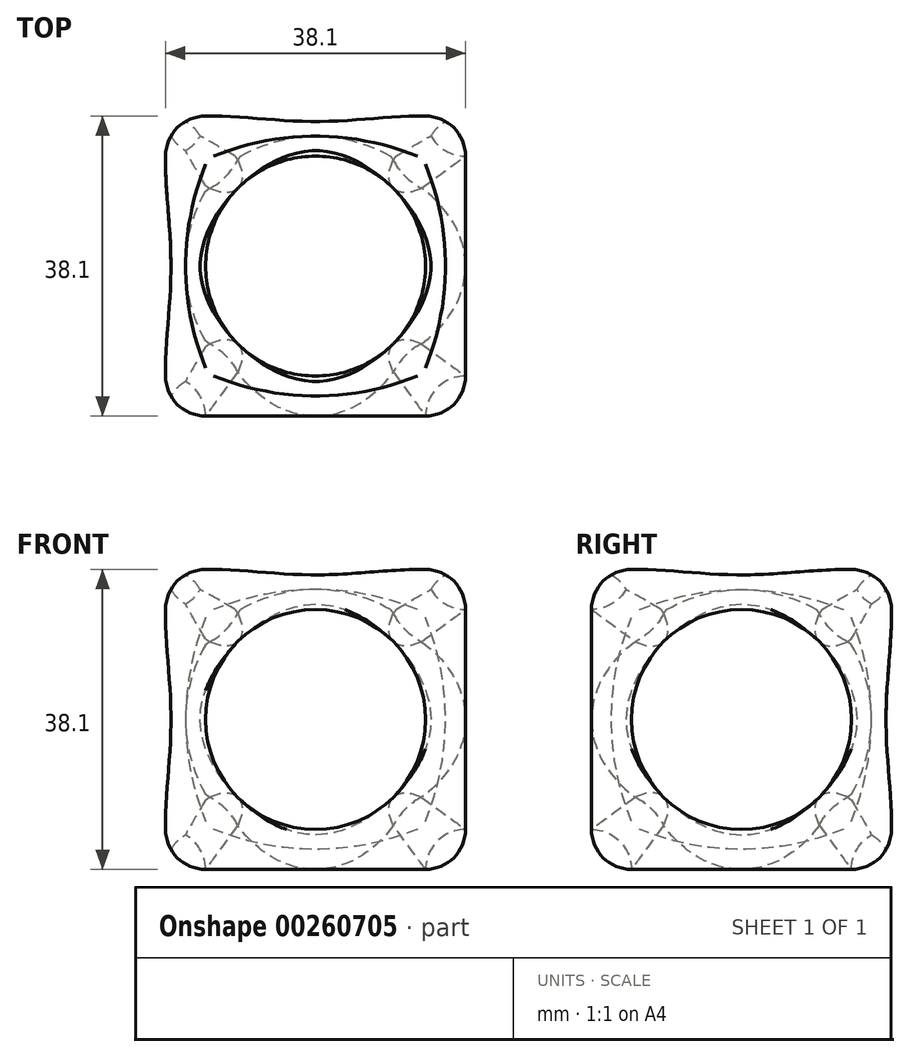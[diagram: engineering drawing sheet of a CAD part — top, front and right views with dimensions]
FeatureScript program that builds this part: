
annotation { "Feature Type Name" : "Feature", "Feature Type Description" : "" }
export const myFeature = defineFeature(function(context is Context, id is Id, definition is map)
    precondition{}
    {
        {
            var Q0;
            Q0=qCreatedBy(makeId("Front.planeOp"),FACE);
            var sketch = newSketch(context, id + "F0", { "sketchPlane" : qUnion([Q0])});
            skLineSegment(sketch, "E0.bottom", {"start": v(-19.05, 19.05) * mm, "end": v(19.05, 19.05) * mm});
            skLineSegment(sketch, "E0.top", {"start": v(-19.05, -19.05) * mm, "end": v(19.05, -19.05) * mm});
            skLineSegment(sketch, "E0.left", {"start": v(-19.05, 19.05) * mm, "end": v(-19.05, -19.05) * mm});
            skLineSegment(sketch, "E0.right", {"start": v(19.05, 19.05) * mm, "end": v(19.05, -19.05) * mm});
            skLineSegment(sketch, "E1", {"start": v(-19.05, 0) * mm, "end": v(0, 0) * mm});
            skLineSegment(sketch, "E2", {"start": v(0, 0) * mm, "end": v(19.05, 0) * mm});
            skLineSegment(sketch, "E3", {"start": v(0, 19.05) * mm, "end": v(0, 0) * mm});
            skLineSegment(sketch, "E4", {"start": v(0, -19.05) * mm, "end": v(0, 0) * mm});
            skSolve(sketch);
        }
        {
            var Q0;
            Q0 = qSketchRegion(id + "F0", true);
            extrude(context, id + "F1", {"entities" : qUnion([Q0]), "endBound" : BoundingType.SYMMETRIC, "depth" : 38.1 * mm});
        }
        {
            var Q0;
            Q0=makeQuery(id+"F1.opExtrude","CAP_FACE",FACE,{"disambiguationData":[OSD([sQuery(id+"F0.wireOp",EDGE,"E0.bottom"),sQuery(id+"F0.wireOp",EDGE,"E0.top"),sQuery(id+"F0.wireOp",EDGE,"E0.left"),sQuery(id+"F0.wireOp",EDGE,"E0.right")])],"isStart":false});
            var sketch = newSketch(context, id + "F2", { "sketchPlane" : qUnion([Q0])});
            skCircle(sketch, "E5", {"center": v(0, 0) * mm, "radius": 13.97 * mm});
            skPoint(sketch, "E5.first.point", {"position": v(0, -13.97) * mm});
            skPoint(sketch, "E5.second.point", {"position": v(-13.97, 0) * mm});
            skPoint(sketch, "E5.third.point", {"position": v(0, 13.97) * mm});
            skSolve(sketch);
        }
        {
            var Q0;
            Q0 = qSketchRegion(id + "F2", true);
            extrude(context, id + "F3", {"entities" : qUnion([Q0]), "operationType" : NewBodyOperationType.REMOVE, "oppositeDirection" : true, "depth" : 76.2 * mm});
        }
        {
            var Q0;
            Q0=makeQuery(id+"F1.opExtrude","SWEPT_FACE",FACE,{"disambiguationData":[OSD([sQuery(id+"F0.wireOp",EDGE,"E0.right")])]});
            var sketch = newSketch(context, id + "F4", { "sketchPlane" : qUnion([Q0])});
            skCircle(sketch, "E6", {"center": v(0, 0) * mm, "radius": 13.97 * mm});
            skPoint(sketch, "E6.first.point", {"position": v(0, -13.97) * mm});
            skPoint(sketch, "E6.second.point", {"position": v(-13.97, 0) * mm});
            skPoint(sketch, "E6.third.point", {"position": v(0, 13.97) * mm});
            skSolve(sketch);
        }
        {
            var Q0;
            Q0 = qSketchRegion(id + "F4", true);
            extrude(context, id + "F5", {"entities" : qUnion([Q0]), "operationType" : NewBodyOperationType.REMOVE, "oppositeDirection" : true, "depth" : 76.2 * mm});
        }
        {
            var Q0;
            Q0=makeQuery(id+"F1.opExtrude","SWEPT_FACE",FACE,{"disambiguationData":[OSD([sQuery(id+"F0.wireOp",EDGE,"E0.top")])]});
            var sketch = newSketch(context, id + "F6", { "sketchPlane" : qUnion([Q0])});
            skCircle(sketch, "E7", {"center": v(0, 0) * mm, "radius": 13.97 * mm});
            skPoint(sketch, "E7.first.point", {"position": v(0, -13.97) * mm});
            skPoint(sketch, "E7.second.point", {"position": v(13.97, 0) * mm});
            skPoint(sketch, "E7.third.point", {"position": v(0, 13.97) * mm});
            skSolve(sketch);
        }
        {
            var Q0;
            Q0 = qSketchRegion(id + "F6", true);
            extrude(context, id + "F7", {"entities" : qUnion([Q0]), "operationType" : NewBodyOperationType.REMOVE, "oppositeDirection" : true, "depth" : 76.2 * mm});
        }
        {
            var Q0;
            Q0=makeQuery(id+"F1.opExtrude","CAP_EDGE",EDGE,{"disambiguationData":[OSD([sQuery(id+"F0.wireOp",EDGE,"E0.bottom")])],"isStart":false});
            var Q1;
            Q1=makeQuery(id+"F1.opExtrude","CAP_EDGE",EDGE,{"disambiguationData":[OSD([sQuery(id+"F0.wireOp",EDGE,"E0.top")])],"isStart":false});
            var Q2;
            Q2=makeQuery(id+"F5.boolean.opBoolean","COPY",EDGE,{"derivedFrom":makeQuery(id+"F5.opExtrude","CAP_EDGE",EDGE,{"disambiguationData":[OSD([sQuery(id+"F4.wireOp",EDGE,"E6")])],"isStart":true})});
            var Q3;
            Q3=makeQuery(id+"F1.opExtrude","SWEPT_EDGE",EDGE,{"disambiguationData":[OSD([sQuery(id+"F0.wireOp",EDGE,"E0.bottom"),sQuery(id+"F0.wireOp",EDGE,"E0.right")])]});
            var Q4;
            Q4=makeQuery(id+"F1.opExtrude","CAP_EDGE",EDGE,{"disambiguationData":[OSD([sQuery(id+"F0.wireOp",EDGE,"E0.right")])],"isStart":false});
            var Q5;
            {var subQ0=makeQuery(id+"F5.opExtrude","SWEPT_FACE",FACE,{"disambiguationData":[OSD([sQuery(id+"F4.wireOp",EDGE,"E6")])]});Q5=makeQuery(id+"F7.boolean.opBoolean","INTERSECT",EDGE,{"disambiguationData":[OD(1.0)],"derivedFrom":[makeQuery(id+"F5.boolean.opBoolean","COPY",FACE,{"disambiguationData":[TD([makeQuery(id+"F1.opExtrude","SWEPT_FACE",FACE,{"disambiguationData":[OSD([sQuery(id+"F0.wireOp",EDGE,"E0.left")])]})])],"derivedFrom":subQ0}),makeQuery(id+"F7.opExtrude","SWEPT_FACE",FACE,{"disambiguationData":[OSD([sQuery(id+"F6.wireOp",EDGE,"E7")])]})]});}
            var Q6;
            Q6=makeQuery(id+"F5.boolean.opBoolean","INTERSECT",EDGE,{"disambiguationData":[OD(2.0)],"derivedFrom":[makeQuery(id+"F3.boolean.opBoolean","COPY",FACE,{"derivedFrom":makeQuery(id+"F3.opExtrude","SWEPT_FACE",FACE,{"disambiguationData":[OSD([sQuery(id+"F2.wireOp",EDGE,"E5")])]})}),makeQuery(id+"F5.opExtrude","SWEPT_FACE",FACE,{"disambiguationData":[OSD([sQuery(id+"F4.wireOp",EDGE,"E6")])]})]});
            var Q7;
            Q7=makeQuery(id+"F1.opExtrude","SWEPT_EDGE",EDGE,{"disambiguationData":[OSD([sQuery(id+"F0.wireOp",EDGE,"E0.bottom"),sQuery(id+"F0.wireOp",EDGE,"E0.left")])]});
            var Q8;
            Q8=makeQuery(id+"F1.opExtrude","SWEPT_EDGE",EDGE,{"disambiguationData":[OSD([sQuery(id+"F0.wireOp",EDGE,"E0.top"),sQuery(id+"F0.wireOp",EDGE,"E0.left")])]});
            var Q9;
            Q9=makeQuery(id+"F1.opExtrude","CAP_EDGE",EDGE,{"disambiguationData":[OSD([sQuery(id+"F0.wireOp",EDGE,"E0.top")])],"isStart":true});
            var Q10;
            Q10=makeQuery(id+"F1.opExtrude","CAP_EDGE",EDGE,{"disambiguationData":[OSD([sQuery(id+"F0.wireOp",EDGE,"E0.left")])],"isStart":false});
            var Q11;
            Q11=makeQuery(id+"F5.boolean.opBoolean","INTERSECT",EDGE,{"derivedFrom":[makeQuery(id+"F1.opExtrude","SWEPT_FACE",FACE,{"disambiguationData":[OSD([sQuery(id+"F0.wireOp",EDGE,"E0.left")])]}),makeQuery(id+"F5.opExtrude","SWEPT_FACE",FACE,{"disambiguationData":[OSD([sQuery(id+"F4.wireOp",EDGE,"E6")])]})]});
            var Q12;
            Q12=makeQuery(id+"F3.boolean.opBoolean","INTERSECT",EDGE,{"derivedFrom":[makeQuery(id+"F1.opExtrude","CAP_FACE",FACE,{"disambiguationData":[OSD([sQuery(id+"F0.wireOp",EDGE,"E0.bottom"),sQuery(id+"F0.wireOp",EDGE,"E0.top"),sQuery(id+"F0.wireOp",EDGE,"E0.left"),sQuery(id+"F0.wireOp",EDGE,"E0.right")])],"isStart":true}),makeQuery(id+"F3.opExtrude","SWEPT_FACE",FACE,{"disambiguationData":[OSD([sQuery(id+"F2.wireOp",EDGE,"E5")])]})]});
            var Q13;
            {var subQ0=makeQuery(id+"F3.boolean.opBoolean","COPY",FACE,{"derivedFrom":makeQuery(id+"F3.opExtrude","SWEPT_FACE",FACE,{"disambiguationData":[OSD([sQuery(id+"F2.wireOp",EDGE,"E5")])]})});Q13=makeQuery(id+"F7.boolean.opBoolean","INTERSECT",EDGE,{"disambiguationData":[OD(0.0)],"derivedFrom":[makeQuery(id+"F5.boolean.opBoolean","SPLIT",FACE,{"disambiguationData":[TD([makeQuery(id+"F1.opExtrude","CAP_FACE",FACE,{"disambiguationData":[OSD([sQuery(id+"F0.wireOp",EDGE,"E0.bottom"),sQuery(id+"F0.wireOp",EDGE,"E0.top"),sQuery(id+"F0.wireOp",EDGE,"E0.left"),sQuery(id+"F0.wireOp",EDGE,"E0.right")])],"isStart":false})])],"derivedFrom":subQ0}),makeQuery(id+"F7.opExtrude","SWEPT_FACE",FACE,{"disambiguationData":[OSD([sQuery(id+"F6.wireOp",EDGE,"E7")])]})]});}
            var Q14;
            {var subQ0=makeQuery(id+"F5.opExtrude","SWEPT_FACE",FACE,{"disambiguationData":[OSD([sQuery(id+"F4.wireOp",EDGE,"E6")])]});Q14=makeQuery(id+"F7.boolean.opBoolean","INTERSECT",EDGE,{"disambiguationData":[OD(0.0)],"derivedFrom":[makeQuery(id+"F5.boolean.opBoolean","COPY",FACE,{"disambiguationData":[TD([makeQuery(id+"F1.opExtrude","SWEPT_FACE",FACE,{"disambiguationData":[OSD([sQuery(id+"F0.wireOp",EDGE,"E0.left")])]})])],"derivedFrom":subQ0}),makeQuery(id+"F7.opExtrude","SWEPT_FACE",FACE,{"disambiguationData":[OSD([sQuery(id+"F6.wireOp",EDGE,"E7")])]})]});}
            var Q15;
            Q15=makeQuery(id+"F1.opExtrude","SWEPT_EDGE",EDGE,{"disambiguationData":[OSD([sQuery(id+"F0.wireOp",EDGE,"E0.top"),sQuery(id+"F0.wireOp",EDGE,"E0.right")])]});
            var Q16;
            {var subQ0=makeQuery(id+"F3.boolean.opBoolean","COPY",FACE,{"derivedFrom":makeQuery(id+"F3.opExtrude","SWEPT_FACE",FACE,{"disambiguationData":[OSD([sQuery(id+"F2.wireOp",EDGE,"E5")])]})});Q16=makeQuery(id+"F7.boolean.opBoolean","INTERSECT",EDGE,{"disambiguationData":[OD(1.0)],"derivedFrom":[makeQuery(id+"F5.boolean.opBoolean","SPLIT",FACE,{"disambiguationData":[TD([makeQuery(id+"F1.opExtrude","CAP_FACE",FACE,{"disambiguationData":[OSD([sQuery(id+"F0.wireOp",EDGE,"E0.bottom"),sQuery(id+"F0.wireOp",EDGE,"E0.top"),sQuery(id+"F0.wireOp",EDGE,"E0.left"),sQuery(id+"F0.wireOp",EDGE,"E0.right")])],"isStart":false})])],"derivedFrom":subQ0}),makeQuery(id+"F7.opExtrude","SWEPT_FACE",FACE,{"disambiguationData":[OSD([sQuery(id+"F6.wireOp",EDGE,"E7")])]})]});}
            var Q17;
            Q17=makeQuery(id+"F1.opExtrude","CAP_EDGE",EDGE,{"disambiguationData":[OSD([sQuery(id+"F0.wireOp",EDGE,"E0.bottom")])],"isStart":true});
            var Q18;
            {var subQ0=makeQuery(id+"F5.opExtrude","SWEPT_FACE",FACE,{"disambiguationData":[OSD([sQuery(id+"F4.wireOp",EDGE,"E6")])]});Q18=makeQuery(id+"F7.boolean.opBoolean","INTERSECT",EDGE,{"disambiguationData":[OD(1.0)],"derivedFrom":[makeQuery(id+"F5.boolean.opBoolean","COPY",FACE,{"disambiguationData":[TD([makeQuery(id+"F1.opExtrude","SWEPT_FACE",FACE,{"disambiguationData":[OSD([sQuery(id+"F0.wireOp",EDGE,"E0.right")])]})])],"derivedFrom":subQ0}),makeQuery(id+"F7.opExtrude","SWEPT_FACE",FACE,{"disambiguationData":[OSD([sQuery(id+"F6.wireOp",EDGE,"E7")])]})]});}
            var Q19;
            Q19=makeQuery(id+"F3.boolean.opBoolean","COPY",EDGE,{"derivedFrom":makeQuery(id+"F3.opExtrude","CAP_EDGE",EDGE,{"disambiguationData":[OSD([sQuery(id+"F2.wireOp",EDGE,"E5")])],"isStart":true})});
            var Q20;
            Q20=makeQuery(id+"F7.boolean.opBoolean","COPY",EDGE,{"derivedFrom":makeQuery(id+"F7.opExtrude","CAP_EDGE",EDGE,{"disambiguationData":[OSD([sQuery(id+"F6.wireOp",EDGE,"E7")])],"isStart":true})});
            var Q21;
            Q21=makeQuery(id+"F1.opExtrude","CAP_EDGE",EDGE,{"disambiguationData":[OSD([sQuery(id+"F0.wireOp",EDGE,"E0.left")])],"isStart":true});
            var Q22;
            Q22=makeQuery(id+"F1.opExtrude","CAP_EDGE",EDGE,{"disambiguationData":[OSD([sQuery(id+"F0.wireOp",EDGE,"E0.right")])],"isStart":true});
            var Q23;
            Q23=makeQuery(id+"F7.boolean.opBoolean","INTERSECT",EDGE,{"derivedFrom":[makeQuery(id+"F1.opExtrude","SWEPT_FACE",FACE,{"disambiguationData":[OSD([sQuery(id+"F0.wireOp",EDGE,"E0.bottom")])]}),makeQuery(id+"F7.opExtrude","SWEPT_FACE",FACE,{"disambiguationData":[OSD([sQuery(id+"F6.wireOp",EDGE,"E7")])]})]});
            var Q24;
            Q24=makeQuery(id+"F5.boolean.opBoolean","INTERSECT",EDGE,{"disambiguationData":[OD(0.0)],"derivedFrom":[makeQuery(id+"F3.boolean.opBoolean","COPY",FACE,{"derivedFrom":makeQuery(id+"F3.opExtrude","SWEPT_FACE",FACE,{"disambiguationData":[OSD([sQuery(id+"F2.wireOp",EDGE,"E5")])]})}),makeQuery(id+"F5.opExtrude","SWEPT_FACE",FACE,{"disambiguationData":[OSD([sQuery(id+"F4.wireOp",EDGE,"E6")])]})]});
            var Q25;
            Q25=makeQuery(id+"F5.boolean.opBoolean","INTERSECT",EDGE,{"disambiguationData":[OD(3.0)],"derivedFrom":[makeQuery(id+"F3.boolean.opBoolean","COPY",FACE,{"derivedFrom":makeQuery(id+"F3.opExtrude","SWEPT_FACE",FACE,{"disambiguationData":[OSD([sQuery(id+"F2.wireOp",EDGE,"E5")])]})}),makeQuery(id+"F5.opExtrude","SWEPT_FACE",FACE,{"disambiguationData":[OSD([sQuery(id+"F4.wireOp",EDGE,"E6")])]})]});
            var Q26;
            Q26=makeQuery(id+"F5.boolean.opBoolean","INTERSECT",EDGE,{"disambiguationData":[OD(1.0)],"derivedFrom":[makeQuery(id+"F3.boolean.opBoolean","COPY",FACE,{"derivedFrom":makeQuery(id+"F3.opExtrude","SWEPT_FACE",FACE,{"disambiguationData":[OSD([sQuery(id+"F2.wireOp",EDGE,"E5")])]})}),makeQuery(id+"F5.opExtrude","SWEPT_FACE",FACE,{"disambiguationData":[OSD([sQuery(id+"F4.wireOp",EDGE,"E6")])]})]});
            var Q27;
            {var subQ0=makeQuery(id+"F5.opExtrude","SWEPT_FACE",FACE,{"disambiguationData":[OSD([sQuery(id+"F4.wireOp",EDGE,"E6")])]});Q27=makeQuery(id+"F7.boolean.opBoolean","INTERSECT",EDGE,{"disambiguationData":[OD(0.0)],"derivedFrom":[makeQuery(id+"F5.boolean.opBoolean","COPY",FACE,{"disambiguationData":[TD([makeQuery(id+"F1.opExtrude","SWEPT_FACE",FACE,{"disambiguationData":[OSD([sQuery(id+"F0.wireOp",EDGE,"E0.right")])]})])],"derivedFrom":subQ0}),makeQuery(id+"F7.opExtrude","SWEPT_FACE",FACE,{"disambiguationData":[OSD([sQuery(id+"F6.wireOp",EDGE,"E7")])]})]});}
            var Q28;
            {var subQ0=makeQuery(id+"F3.boolean.opBoolean","COPY",FACE,{"derivedFrom":makeQuery(id+"F3.opExtrude","SWEPT_FACE",FACE,{"disambiguationData":[OSD([sQuery(id+"F2.wireOp",EDGE,"E5")])]})});Q28=makeQuery(id+"F7.boolean.opBoolean","INTERSECT",EDGE,{"disambiguationData":[OD(0.0)],"derivedFrom":[makeQuery(id+"F5.boolean.opBoolean","SPLIT",FACE,{"disambiguationData":[TD([makeQuery(id+"F1.opExtrude","CAP_FACE",FACE,{"disambiguationData":[OSD([sQuery(id+"F0.wireOp",EDGE,"E0.bottom"),sQuery(id+"F0.wireOp",EDGE,"E0.top"),sQuery(id+"F0.wireOp",EDGE,"E0.left"),sQuery(id+"F0.wireOp",EDGE,"E0.right")])],"isStart":true})])],"derivedFrom":subQ0}),makeQuery(id+"F7.opExtrude","SWEPT_FACE",FACE,{"disambiguationData":[OSD([sQuery(id+"F6.wireOp",EDGE,"E7")])]})]});}
            var Q29;
            {var subQ0=makeQuery(id+"F3.boolean.opBoolean","COPY",FACE,{"derivedFrom":makeQuery(id+"F3.opExtrude","SWEPT_FACE",FACE,{"disambiguationData":[OSD([sQuery(id+"F2.wireOp",EDGE,"E5")])]})});Q29=makeQuery(id+"F7.boolean.opBoolean","INTERSECT",EDGE,{"disambiguationData":[OD(1.0)],"derivedFrom":[makeQuery(id+"F5.boolean.opBoolean","SPLIT",FACE,{"disambiguationData":[TD([makeQuery(id+"F1.opExtrude","CAP_FACE",FACE,{"disambiguationData":[OSD([sQuery(id+"F0.wireOp",EDGE,"E0.bottom"),sQuery(id+"F0.wireOp",EDGE,"E0.top"),sQuery(id+"F0.wireOp",EDGE,"E0.left"),sQuery(id+"F0.wireOp",EDGE,"E0.right")])],"isStart":true})])],"derivedFrom":subQ0}),makeQuery(id+"F7.opExtrude","SWEPT_FACE",FACE,{"disambiguationData":[OSD([sQuery(id+"F6.wireOp",EDGE,"E7")])]})]});}
            fillet(context, id + "F8", {"entities" : qUnion([Q0, Q1, Q2, Q3, Q4, Q5, Q6, Q7, Q8, Q9, Q10, Q11, Q12, Q13, Q14, Q15, Q16, Q17, Q18, Q19, Q20, Q21, Q22, Q23, Q24, Q25, Q26, Q27, Q28, Q29]), "radius" : 5.08 * mm, "tangentPropagation" : true, "allowEdgeOverflow" : false});
        }
    });
